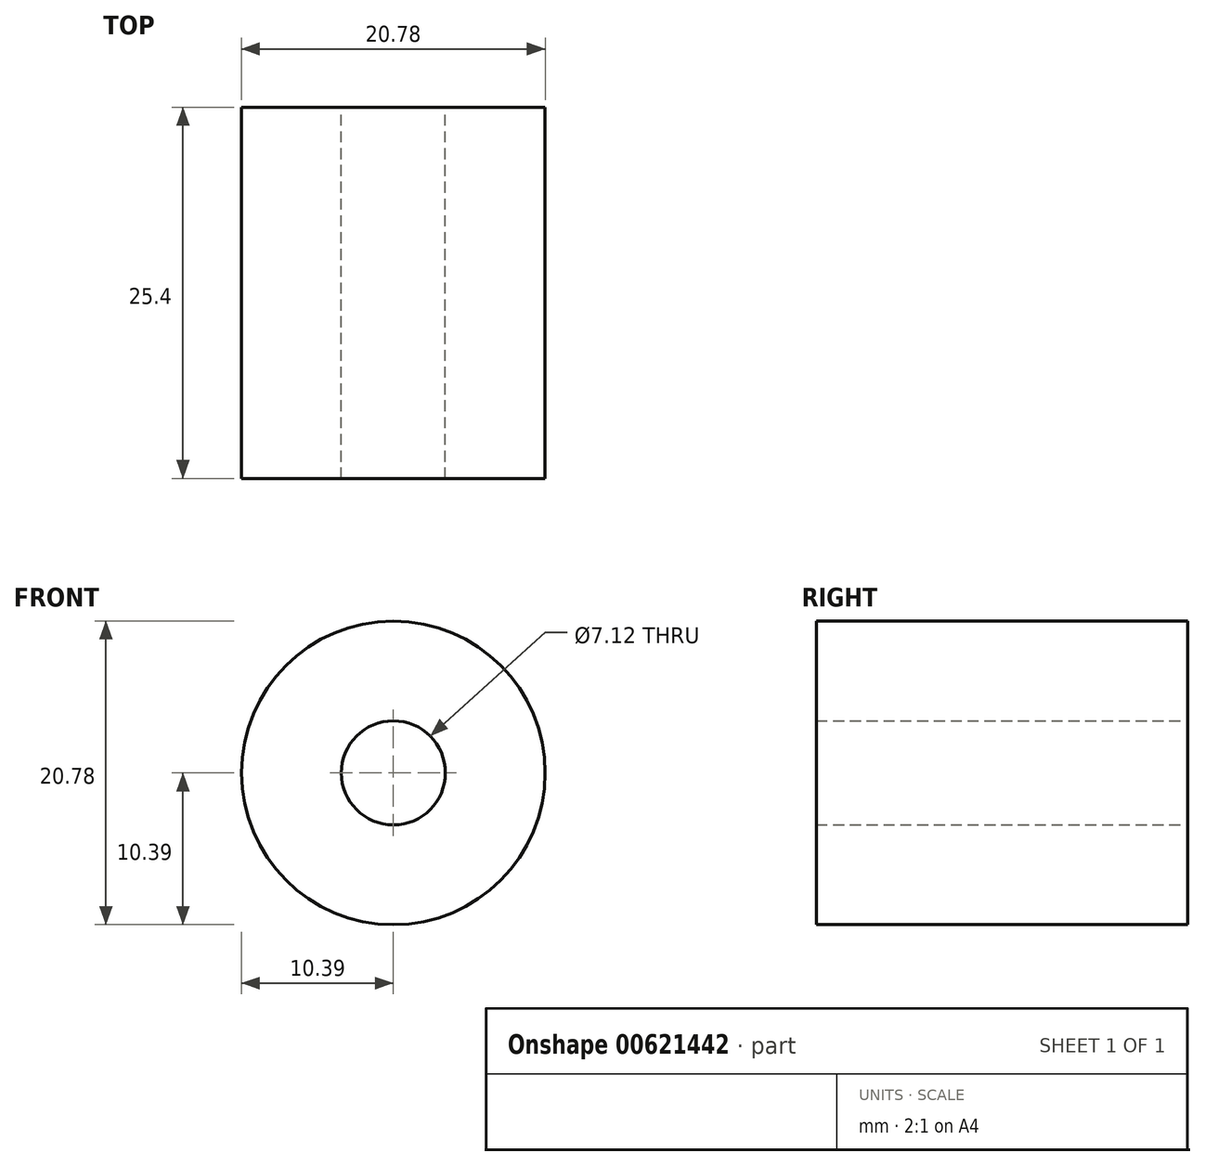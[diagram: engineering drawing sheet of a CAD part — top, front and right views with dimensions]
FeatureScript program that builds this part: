
annotation { "Feature Type Name" : "Feature", "Feature Type Description" : "" }
export const myFeature = defineFeature(function(context is Context, id is Id, definition is map)
    precondition{}
    {
        {
            var Q0;
            Q0=qCreatedBy(makeId("Front.planeOp"),FACE);
            var sketch = newSketch(context, id + "F0", { "sketchPlane" : qUnion([Q0])});
            skCircle(sketch, "E0", {"center": v(0, 0) * mm, "radius": 10.39 * mm});
            skCircle(sketch, "E1", {"center": v(0, 0) * mm, "radius": 3.56 * mm});
            skSolve(sketch);
        }
        {
            var Q0;
            Q0 = qSketchRegion(id + "F0", true);
            extrude(context, id + "F1", {"entities" : qUnion([Q0]), "depth" : 25.4 * mm, "offsetDistance" : 25.4 * mm});
        }
    });
